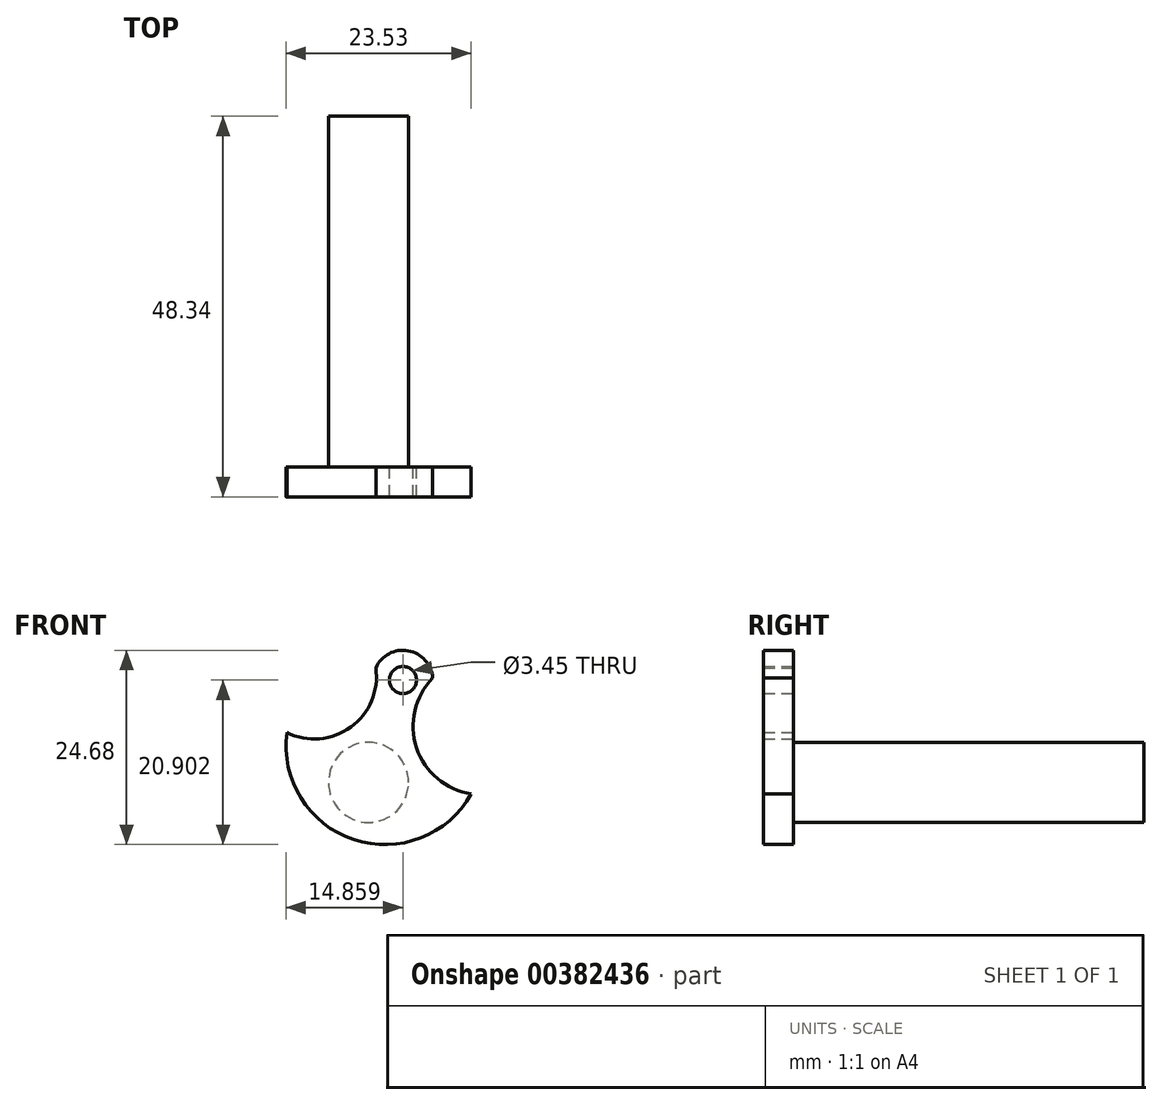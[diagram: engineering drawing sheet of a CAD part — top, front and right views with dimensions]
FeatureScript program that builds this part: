
annotation { "Feature Type Name" : "Feature", "Feature Type Description" : "" }
export const myFeature = defineFeature(function(context is Context, id is Id, definition is map)
    precondition{}
    {
        {
            var Q0;
            Q0=qCreatedBy(makeId("Front.planeOp"),FACE);
            var sketch = newSketch(context, id + "F0", { "sketchPlane" : qUnion([Q0])});
            skArc(sketch, "E0", {"start": v(-51.99, 25.76) * mm, "mid": v(-43.5, 12.18) * mm, "end": v(-28.57, 17.98) * mm});
            skArc(sketch, "E1", {"start": v(-33.47, 32.7) * mm, "mid": v(-35.5, 23.84) * mm, "end": v(-28.57, 17.98) * mm});
            skArc(sketch, "E2", {"start": v(-51.99, 25.76) * mm, "mid": v(-43.86, 26.48) * mm, "end": v(-40.68, 34) * mm});
            skArc(sketch, "E3", {"start": v(-33.47, 32.7) * mm, "mid": v(-36.57, 36.16) * mm, "end": v(-40.68, 34) * mm});
            skCircle(sketch, "E4", {"center": v(-37.24, 32.44) * mm, "radius": 1.72 * mm});
            skSolve(sketch);
        }
        {
            var Q0;
            Q0=makeQuery(id+"F0.imprint","IMPRINT",FACE,{"disambiguationData":[TD([[makeQuery(id+"F0.imprint","IMPRINT",EDGE,{"derivedFrom":sQuery(id+"F0.wireOp",EDGE,"E0")}),1.0]])]});
            extrude(context, id + "F1", {"entities" : qUnion([Q0]), "depth" : 3.8 * mm});
        }
        {
            var Q0;
            Q0=qCreatedBy(makeId("Front.planeOp"),FACE);
            var sketch = newSketch(context, id + "F2", { "sketchPlane" : qUnion([Q0])});
            skCircle(sketch, "E5", {"center": v(-41.61, 19.44) * mm, "radius": 5.08 * mm});
            skSolve(sketch);
        }
        {
            var Q0;
            Q0=makeQuery(id+"F2.imprint","IMPRINT",FACE,{"disambiguationData":[TD([[makeQuery(id+"F2.imprint","IMPRINT",EDGE,{"derivedFrom":sQuery(id+"F2.wireOp",EDGE,"E5")}),1.0]])]});
            extrude(context, id + "F3", {"entities" : qUnion([Q0]), "operationType" : NewBodyOperationType.ADD, "oppositeDirection" : true, "depth" : 1.88 * mm});
        }
        {
            var Q0;
            Q0=qCreatedBy(makeId("Front.planeOp"),FACE);
            var sketch = newSketch(context, id + "F4", { "sketchPlane" : qUnion([Q0])});
            skCircle(sketch, "E6", {"center": v(-41.71, 19.8) * mm, "radius": 4.08 * mm});
            skSolve(sketch);
        }
        {
            var Q0;
            Q0=makeQuery(id+"F3.opExtrude","CAP_FACE",FACE,{"disambiguationData":[OSD([sQuery(id+"F2.wireOp",EDGE,"E5")])],"isStart":false});
            extrude(context, id + "F5", {"entities" : qUnion([Q0]), "operationType" : NewBodyOperationType.ADD, "depth" : 1.8 * mm});
        }
        {
            var Q0;
            Q0=makeQuery(id+"F5.opExtrude","CAP_FACE",FACE,{"disambiguationData":[OSD([sQuery(id+"F2.wireOp",EDGE,"E5")])],"isStart":false});
            var Q1;
            Q1=makeQuery(id+"F4.imprint","IMPRINT",FACE,{"disambiguationData":[TD([[makeQuery(id+"F4.imprint","IMPRINT",EDGE,{"derivedFrom":sQuery(id+"F4.wireOp",EDGE,"E6")}),1.0]])]});
            var Q2;
            Q2=makeQuery(id+"F1.opExtrude","CAP_FACE",FACE,{"disambiguationData":[OSD([sQuery(id+"F0.wireOp",EDGE,"E0"),sQuery(id+"F0.wireOp",EDGE,"E1"),sQuery(id+"F0.wireOp",EDGE,"E2"),sQuery(id+"F0.wireOp",EDGE,"E3"),sQuery(id+"F0.wireOp",EDGE,"E4")])],"isStart":false});
            extrude(context, id + "F6", {"entities" : qUnion([Q0, Q1, Q2]), "operationType" : NewBodyOperationType.ADD, "depth" : 0.2 * mm});
        }
        {
            var Q0;
            Q0=makeQuery(id+"F6.opExtrude","CAP_FACE",FACE,{"disambiguationData":[OSD([sQuery(id+"F2.wireOp",EDGE,"E5")])],"isStart":false});
            extrude(context, id + "F7", {"entities" : qUnion([Q0]), "operationType" : NewBodyOperationType.ADD, "depth" : 40.64 * mm});
        }
    });
